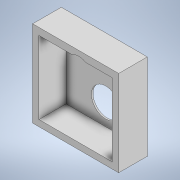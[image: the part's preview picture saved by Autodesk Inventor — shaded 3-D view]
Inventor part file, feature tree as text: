
AUTODESK INVENTOR PART (.ipt)
format: ipt  version: 2022 (Build 260153000, 153)  size: 115,200 bytes
history: native  units: mm
features: extrude x3, sketch x3
ambient origin geometry x8: Origin, YZ Plane, XZ Plane, XY Plane, X Axis, Y Axis, Z Axis, Center Point
bodies: Solid1 (feature_tree)
feature tree (6):
  extrude  "Extrusion1"  Depth=114.3mm
  extrude  "Extrusion2"  Depth=36.0mm TaperAngle=0.0deg
  extrude  "Extrusion3"  Depth=38.1mm
  sketch  "Sketch1"  dims[d0=114.3mm d1=114.3mm]
  sketch  "Sketch2"  dims[d2=38.1mm d3=0.0mm d4=36.0mm d5=0.0mm]
  sketch  "Sketch3"  dims[d6=38.1mm d7=38.1mm d8=0.0mm d9=0.0mm]
